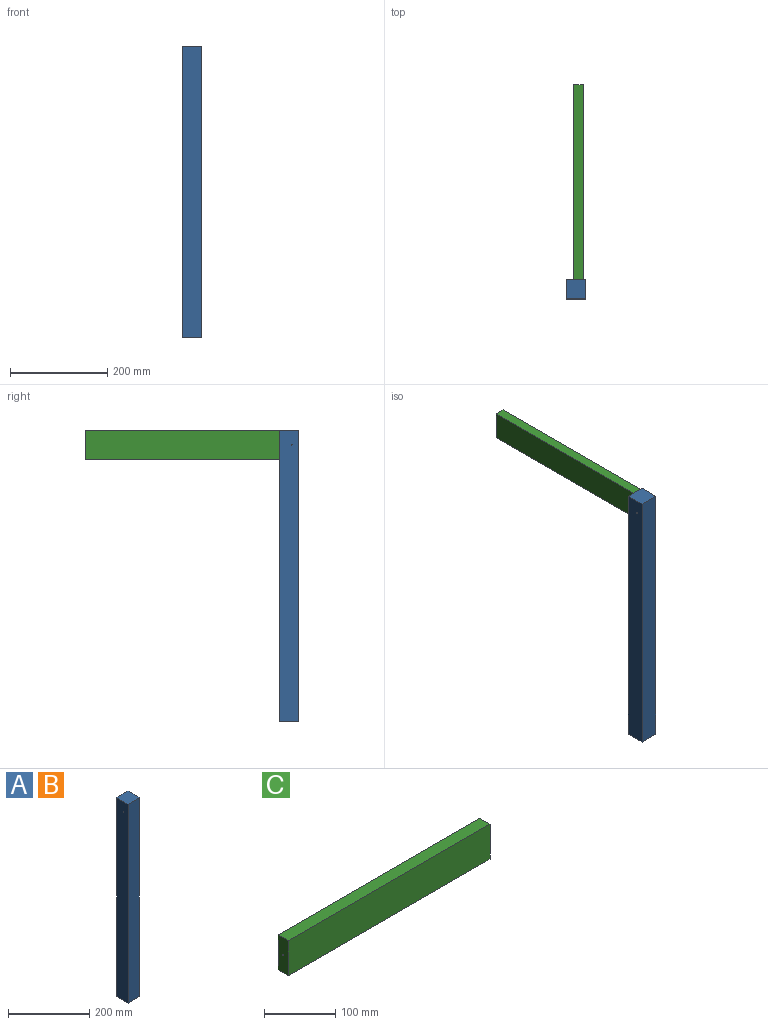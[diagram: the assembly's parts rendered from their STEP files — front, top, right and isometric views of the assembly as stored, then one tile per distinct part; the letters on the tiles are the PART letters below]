
ASSEMBLY  parts=3 mates=1
PART A: 10 faces, bbox 40x40x600 mm
  f0: plane 600x40mm, normal (1,0,0), area 24000mm2, adj f1,f3,f4,f5
  f1: plane 600x40mm, normal (0,1,0), area 23996.9mm2, adj f0,f2,f4,f5,f8
  f2: plane 600x40mm, normal (-1,0,0), area 23996.9mm2, adj f1,f3,f4,f5,f6
  f3: plane 600x40mm, normal (0,-1,0), area 24000mm2, adj f0,f2,f4,f5
  f4: plane 40x40mm, normal (0,0,1), area 1600mm2, adj f0,f1,f2,f3
  f5: plane 40x40mm, normal (0,0,-1), area 1600mm2, adj f0,f1,f2,f3
  f6: cylinder r=1mm len=5mm, axis (-1,0,0), area 31.4mm2, adj f2,f7
  f7: plane 2x2mm, normal (-1,0,0), area 3.1mm2, adj f6
  f8: cylinder r=1mm len=5mm, axis (0,1,0), area 31.4mm2, adj f1,f9
  f9: plane 2x2mm, normal (0,1,0), area 3.1mm2, adj f8
PART B: same geometry as A
PART C: 10 faces, bbox 400x20x60 mm
  f0: plane 400x60mm, normal (0,1,0), area 24000mm2, adj f1,f3,f4,f5
  f1: plane 400x20mm, normal (0,0,1), area 8000mm2, adj f0,f2,f4,f5
  f2: plane 400x60mm, normal (0,-1,0), area 24000mm2, adj f1,f3,f4,f5
  f3: plane 400x20mm, normal (0,0,-1), area 8000mm2, adj f0,f2,f4,f5
  f4: plane 60x20mm, normal (1,0,0), area 1196.9mm2, adj f0,f1,f2,f3,f6
  f5: plane 60x20mm, normal (-1,0,0), area 1196.9mm2, adj f0,f1,f2,f3,f8
  f6: cylinder r=1mm len=5mm, axis (1,0,0), area 31.4mm2, adj f4,f7
  f7: plane 2x2mm, normal (1,0,0), area 3.1mm2, adj f6
  f8: cylinder r=1mm len=5mm, axis (-1,0,0), area 31.4mm2, adj f5,f9
  f9: plane 2x2mm, normal (-1,0,0), area 3.1mm2, adj f8
PLACE A t=(-134.86,-83.35,-8.23)mm fixed
PLACE B t=(-134.86,-83.35,-8.23)mm
PLACE C rot(axis=(0,0,1),90deg) t=(-129.86,136.65,261.77)mm
MATE fastened C.f6 <-> A.f8  axis (0,-1,0) through (-129.86,-63.35,261.77)mm
